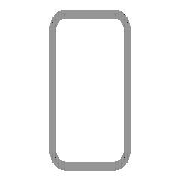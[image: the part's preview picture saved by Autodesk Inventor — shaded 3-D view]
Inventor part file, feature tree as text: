
AUTODESK INVENTOR PART (.ipt)
format: ipt  version: 2025 (Build 290162010, 162A)  size: 133,120 bytes
history: native  units: mm (DEFAULTED — no unit token found)
features: other x4, sketch x1, plane x1
ambient origin geometry x8: Origin, YZ Plane, XZ Plane, XY Plane, X Axis, Y Axis, Z Axis, Center Point
bodies: Solid1 (feature_tree), Body (feature_tree)
feature tree (6):
  parser-record x1  (decoder bookkeeping rows leaked as tree rows — omitted from the tree; the rows remain in map.json)
  other  "Driven Length"
  other  "Start Plane"
  other  "End Plane"
  sketch  "Sketch3"  dims[d3=1020.0mm d4=0.0mm d7=6.0mm d9=40.0mm d11=60.0mm d12=3.0mm d13=40.0mm d14=1060.0mm d15=20.0mm d16=30.0mm d17=90.0deg d18=1020.0mm]
  plane  "Work Plane3"
